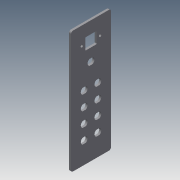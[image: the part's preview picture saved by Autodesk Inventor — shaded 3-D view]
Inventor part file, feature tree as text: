
AUTODESK INVENTOR PART (.ipt)
format: ipt  version: 2015 SP1 (Build 190203100, 203)  size: 231,936 bytes
history: native  units: mm
features: extrude x4, sketch x4, fillet x2, hole x1, projected_geometry x1
ambient origin geometry x8: Origin, YZ Plane, XZ Plane, XY Plane, X Axis, Y Axis, Z Axis, Center Point
bodies: Solid1 (feature_tree)
feature tree (12):
  extrude  "Extrusion1"  Depth=55.6mm
  fillet  "Fillet1"  Radius=3.0mm
  extrude  "Extrusion2"  Depth=3.0mm
  sketch  "Sketch4"  dims[d6=45.0mm d9=169.5mm d10=9.75mm]
  extrude  "Extrusion3"  Depth=169.5mm
  fillet  "Fillet2"  Radius=9.75mm
  hole  "Hole4"  [1 undecoded]
  extrude  "Extrusion4"  Depth=1.0mm TaperAngle=0.0deg
  sketch  "Sketch1"  dims[d0=169.5mm d1=55.6mm d2=3.0mm d3=0.0mm]
  sketch  "Sketch2"  dims[d4=3.0mm d5=150.0mm]
  sketch  "Sketch9"  dims[d11=55.6mm d12=5.3mm d13=0.1mm d14=0.0mm d16=20.0mm d17=20.0mm d18=20.0mm d20=19.0mm d25=20.0mm d26=20.0mm d27=20.0mm d28=19.0mm d29=19.0mm d43=13.0mm d44=45.0mm d45=13.0mm d46=13.0mm d47=13.0mm d70=22.5mm d71=8.3mm d72=4.75mm d73=40.0mm d74=20.189156mm d75=8.3mm d76=4.75mm d77=8.3mm d78=4.75mm d79=8.3mm d81=8.3mm d82=8.3mm d83=8.3mm d84=8.3mm d85=4.75mm d86=4.75mm d88=4.75mm d90=4.75mm d98=20.0mm d100=20.0mm d101=8.3mm d102=20.0mm d103=0.0mm d104=16.0mm d105=16.0mm d106=15.0mm d107=22.5mm d108=8.0mm d109=8.0mm d110=12.7mm d111=12.7mm d119=1.0mm d120=3.4mm d121=5.69mm d122=3.023mm d123=2.0mm d124=14.3117mm d125=8.865mm d126=20.594885mm d127=0.1mm d128=0.0mm]
  projected_geometry  "Projected Loop1"
note: 1 required parameter value undecoded (feature->parameter linkage not recoverable at this tier; creation-order binding heuristic only, values carry confidence <= 0.55)
